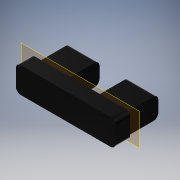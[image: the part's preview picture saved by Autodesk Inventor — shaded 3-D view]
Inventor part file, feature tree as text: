
AUTODESK INVENTOR PART (.ipt)
format: ipt  version: 2018 (Build 220112000, 112)  size: 150,528 bytes
history: native  units: mm
features: other x3, extrude x2, sketch x2, reference x2, plane x1, fillet x1
ambient origin geometry x8: Origin, YZ Plane, XZ Plane, XY Plane, X Axis, Y Axis, Z Axis, Center Point
bodies: Body1 (feature_tree)
feature tree (11):
  plane  "Work Plane1"
  extrude  "Extrusion3"  Depth=0.8mm
  extrude  "Extrusion4"  Depth=3.0mm TaperAngle=0.0deg
  fillet  "Fillet6"  Radius=0.5mm
  sketch  "Sketch3"  dims[d26=0.8mm d27=0.8mm]
  reference  "Reference15"
  sketch  "Sketch4"  dims[d28=0.7mm d29=3.0mm d30=0.0mm d31=0.5mm d32=0.5mm d33=0.7mm d34=0.7mm d35=0.5mm d36=0.5mm d37=7.0mm d38=0.0mm d39=1.0mm d40=1.0mm]
  reference  "Reference16"
  other  "<userpath>\Dropbox\Skola\Projekt\Kretsn_Brillz_V2\3D\Main.iam"
  other  "Main.iam"
  other  "Holster_Top_V2:1"
